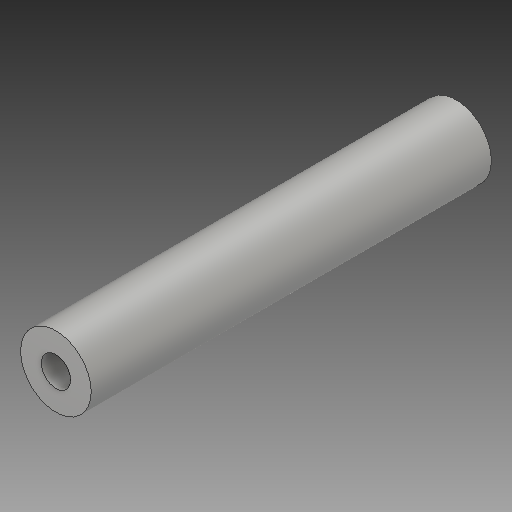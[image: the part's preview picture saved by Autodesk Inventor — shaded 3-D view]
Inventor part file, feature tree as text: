
AUTODESK INVENTOR PART (.ipt)
format: ipt  version: 2019 (Build 230136000, 136)  size: 95,744 bytes
history: native  units: mm
features: extrude x1, sketch x1
ambient origin geometry x8: Origin, YZ Plane, XZ Plane, XY Plane, X Axis, Y Axis, Z Axis, Center Point
bodies: Solid1 (feature_tree)
feature tree (2):
  extrude  "Extrusion1"  Depth=68.0mm
  sketch  "Sketch1"  dims[d0=5.0mm d1=12.0mm d2=68.0mm d3=0.0mm]
